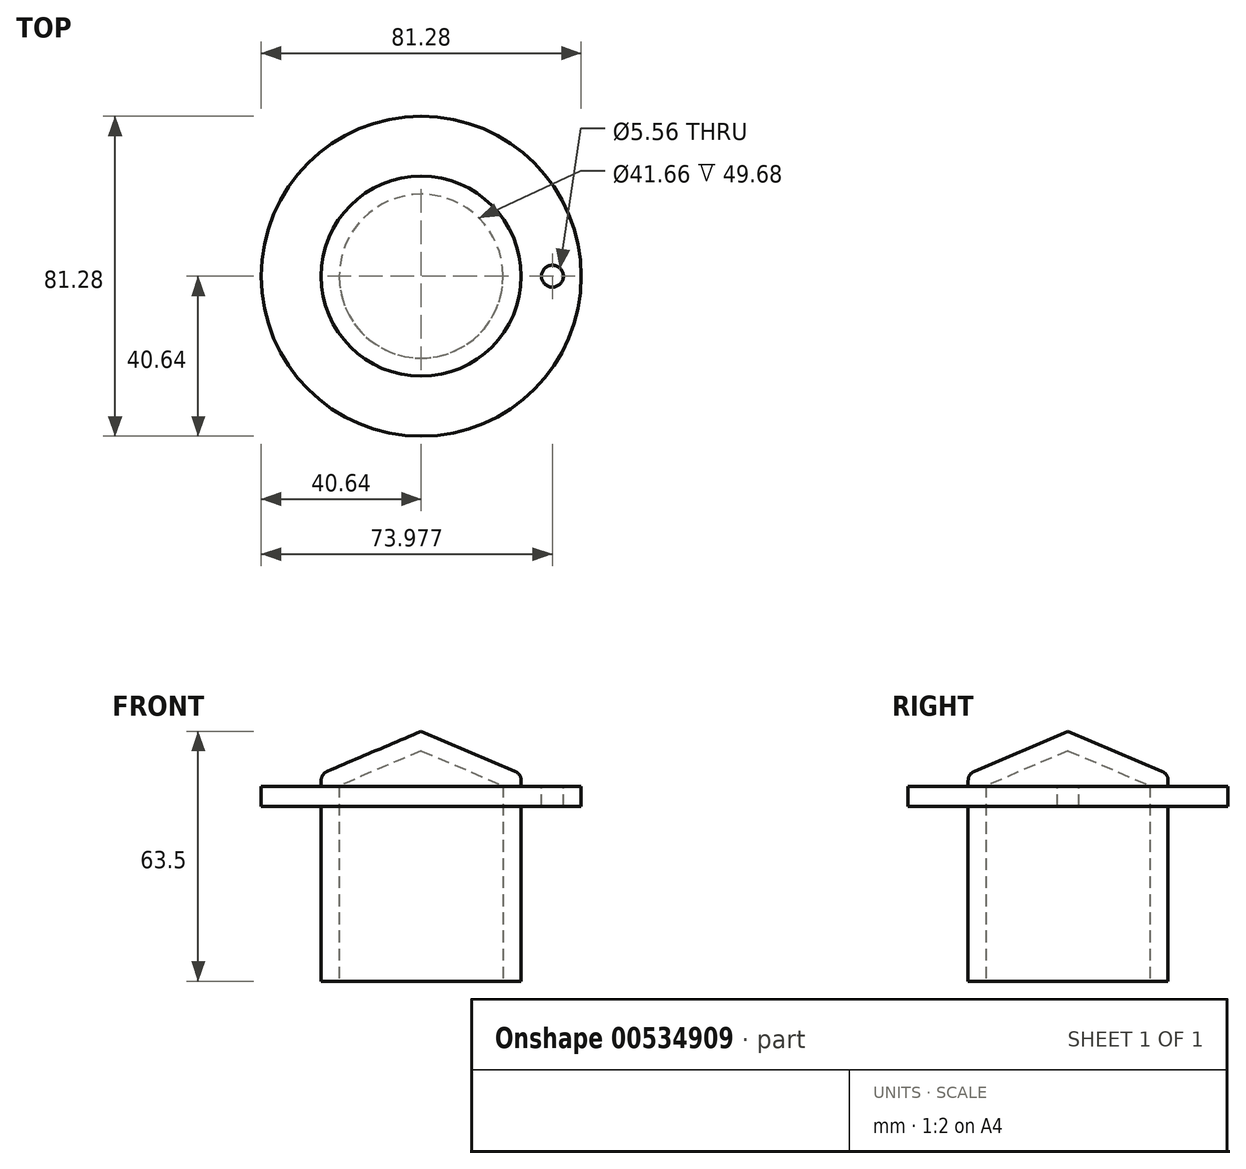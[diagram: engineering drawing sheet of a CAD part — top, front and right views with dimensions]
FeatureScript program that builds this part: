
annotation { "Feature Type Name" : "Feature", "Feature Type Description" : "" }
export const myFeature = defineFeature(function(context is Context, id is Id, definition is map)
    precondition{}
    {
        {
            var Q0;
            Q0=qCreatedBy(makeId("Top.planeOp"),FACE);
            var sketch = newSketch(context, id + "F0", { "sketchPlane" : qUnion([Q0])});
            skCircle(sketch, "E0", {"center": v(0, 0) * mm, "radius": 33.34 * mm, "construction": true});
            skPoint(sketch, "E1", {"position": v(33.34, 0) * mm});
            skSolve(sketch);
        }
        {
            var Q0;
            Q0=qCreatedBy(makeId("Front.planeOp"),FACE);
            var sketch = newSketch(context, id + "F1", { "sketchPlane" : qUnion([Q0])});
            skLineSegment(sketch, "E2", {"start": v(0, 19.05) * mm, "end": v(25.4, 8.25) * mm});
            skLineSegment(sketch, "E3", {"start": v(25.4, 8.25) * mm, "end": v(25.4, 5.08) * mm});
            skLineSegment(sketch, "E4", {"start": v(25.4, 5.08) * mm, "end": v(40.64, 5.08) * mm});
            skLineSegment(sketch, "E5", {"start": v(40.64, 5.08) * mm, "end": v(40.64, 0) * mm});
            skLineSegment(sketch, "E6", {"start": v(40.64, 0) * mm, "end": v(25.4, 0) * mm});
            skLineSegment(sketch, "E7", {"start": v(25.4, 0) * mm, "end": v(25.4, -44.45) * mm});
            skLineSegment(sketch, "E8", {"start": v(25.4, -44.45) * mm, "end": v(0, -44.45) * mm});
            skLineSegment(sketch, "E9", {"start": v(0, -44.45) * mm, "end": v(0, 19.05) * mm});
            skLineSegment(sketch, "E10", {"start": v(0, -44.45) * mm, "end": v(0, 22.16) * mm, "construction": true});
            skSolve(sketch);
        }
        {
            var Q0;
            Q0=makeQuery(id+"F1.imprint","IMPRINT",FACE,{"disambiguationData":[TD([[makeQuery(id+"F1.imprint","IMPRINT",EDGE,{"derivedFrom":sQuery(id+"F1.wireOp",EDGE,"E2")}),-1.0]])]});
            var Q1;
            Q1 = qSketchRegion(id + "F0", true);
            var Q2;
            Q2=sQuery(id+"F1.wireOp",EDGE,"E9");
            revolve(context, id + "F2", {"entities" : qUnion([Q0, Q1]), "axis" : qUnion([Q2]), "revolveType" : RevolveType.FULL});
        }
        {
            var Q0;
            Q0=sQuery(id+"F0.wireOp",VERTEX,"E1");
            var Q1;
            Q1=makeQuery(id+"F2.opRevolve","SWEPT_BODY",BODY,{"disambiguationData":[OSD([sQuery(id+"F1.wireOp",EDGE,"E2"),sQuery(id+"F1.wireOp",EDGE,"E3"),sQuery(id+"F1.wireOp",EDGE,"E4"),sQuery(id+"F1.wireOp",EDGE,"E5"),sQuery(id+"F1.wireOp",EDGE,"E6"),sQuery(id+"F1.wireOp",EDGE,"E7"),sQuery(id+"F1.wireOp",EDGE,"E8"),sQuery(id+"F1.wireOp",EDGE,"RNC5RQLm-zhN8-w61K-d9Pd-YudIvvWRg4jQ"),sQuery(id+"F1.wireOp",EDGE,"QPxZvhh9-nHpU-of6s-mdia-goPWyIfZ9gv4"),sQuery(id+"F1.wireOp",EDGE,"E9")])]});
            hole(context, id + "F3", {"style" : HoleStyle.SIMPLE, "endStyle" : HoleEndStyle.THROUGH, "oppositeDirection" : true, "holeDiameter" : 5.56 * mm, "isTappedThrough" : true, "tappedDepth" : 12.7 * mm, "tapClearance" : 3, "locations" : qUnion([Q0]), "scope" : qUnion([Q1]), "startStyle" : HoleStartStyle.PART});
        }
        {
            var Q0;
            Q0=makeQuery(id+"F2.opRevolve","SWEPT_EDGE",EDGE,{"disambiguationData":[OSD([sQuery(id+"F1.wireOp",EDGE,"E2"),sQuery(id+"F1.wireOp",EDGE,"E3")])]});
            fillet(context, id + "F4", {"entities" : qUnion([Q0]), "radius" : 2.54 * mm, "tangentPropagation" : true, "allowEdgeOverflow" : false});
        }
        {
            var Q0;
            Q0=makeQuery(id+"F2.opRevolve","SWEPT_FACE",FACE,{"disambiguationData":[OSD([sQuery(id+"F1.wireOp",EDGE,"E8")])]});
            shell(context, id + "F5", {"entities" : qUnion([Q0]), "thickness" : 4.57 * mm});
        }
    });
